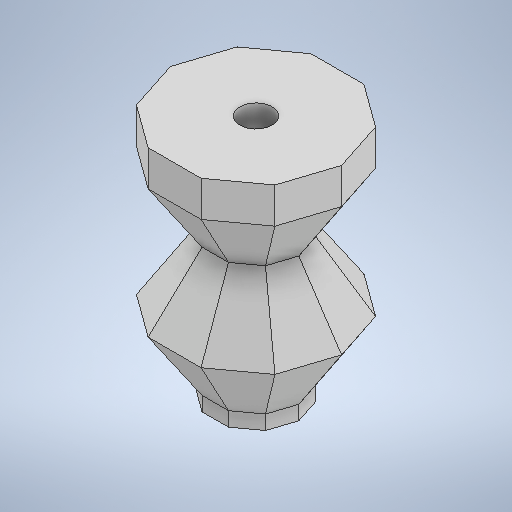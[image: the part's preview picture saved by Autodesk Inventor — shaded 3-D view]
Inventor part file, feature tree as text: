
AUTODESK INVENTOR PART (.ipt)
format: ipt  version: 2025.1 (Build 291241000, 241)  size: 333,824 bytes
history: native  units: mm
features: sketch x5, other x3, extrude x3, mirror x2, projected_geometry x2, loft x1, shell x1
ambient origin geometry x8: Origin, YZ Plane, XZ Plane, XY Plane, X Axis, Y Axis, Z Axis, Center Point
bodies: Body1 (feature_tree)
feature tree (17):
  other  "솔리드1"
  sketch  "스케치1"
  other  "작업 평면1"
  loft  "로프트1"
  other  "작업 평면2"
  mirror  "미러1"
  mirror  "미러2"
  shell  "쉘1"  Thickness=9.0mm
  extrude  "돌출1"  Depth=12.0mm
  extrude  "돌출2"  TaperAngle=0.0deg  [1 undecoded]
  extrude  "돌출3"  TaperAngle=0.0deg  [1 undecoded]
  sketch  "스케치2"
  sketch  "스케치3"
  projected_geometry  "투영된 루프1"
  sketch  "스케치4"
  projected_geometry  "투영된 루프2"
  sketch  "스케치5"
note: 2 required parameter values undecoded (feature->parameter linkage not recoverable at this tier; creation-order binding heuristic only, values carry confidence <= 0.55)
